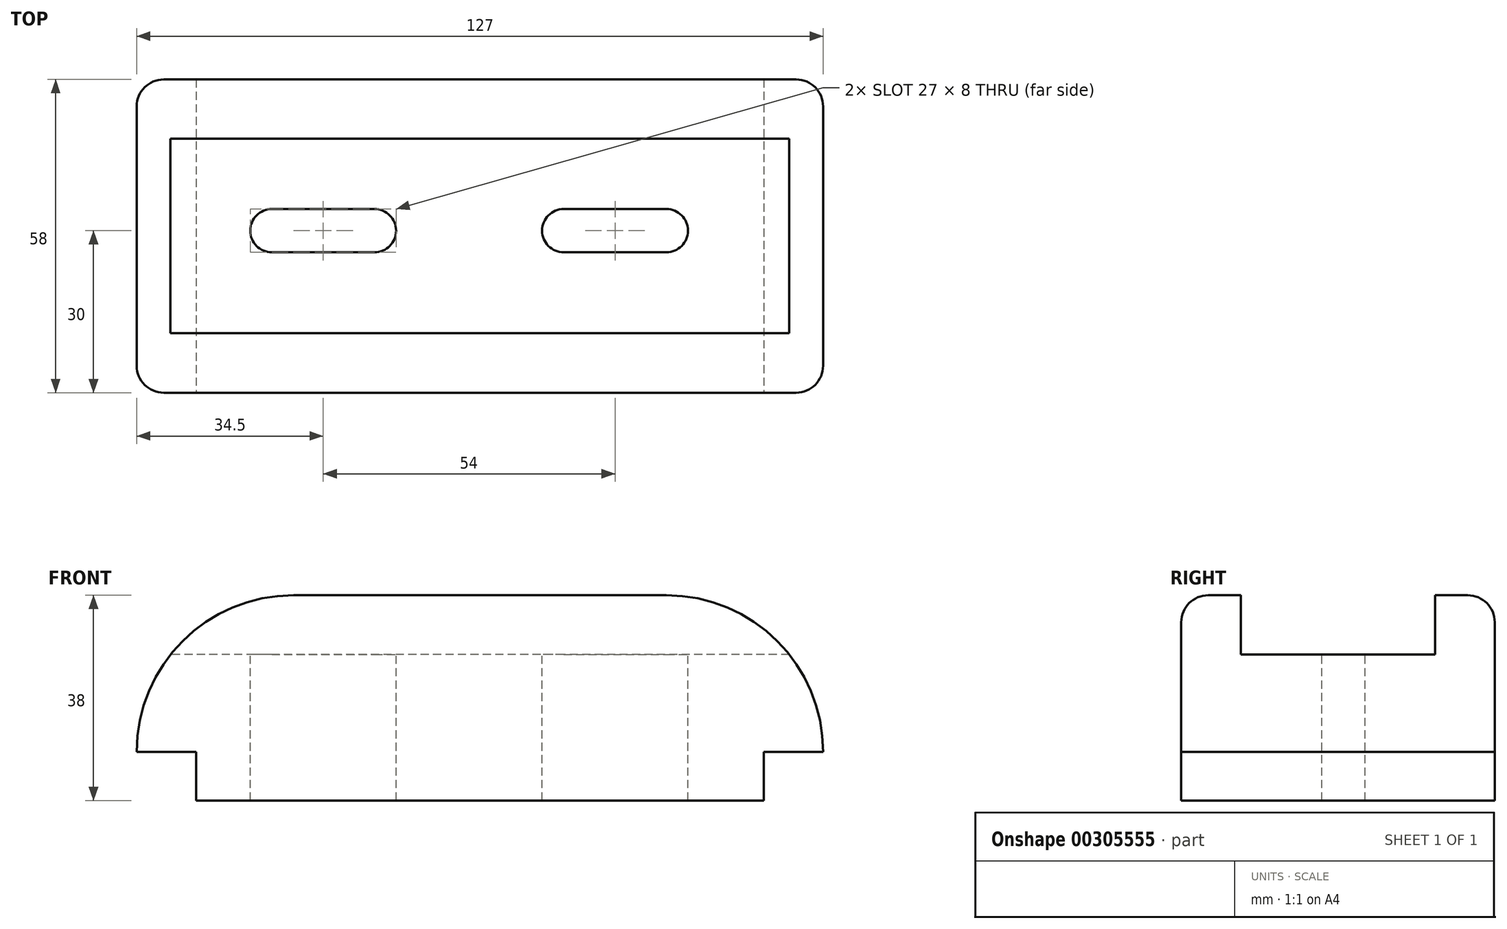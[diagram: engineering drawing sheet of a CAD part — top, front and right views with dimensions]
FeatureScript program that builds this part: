
annotation { "Feature Type Name" : "Feature", "Feature Type Description" : "" }
export const myFeature = defineFeature(function(context is Context, id is Id, definition is map)
    precondition{}
    {
        {
            var Q0;
            Q0=qCreatedBy(makeId("Front.planeOp"),FACE);
            var sketch = newSketch(context, id + "F0", { "sketchPlane" : qUnion([Q0])});
            skLineSegment(sketch, "E0.bottom", {"start": v(0, 0) * mm, "end": v(127, 0) * mm});
            skLineSegment(sketch, "E0.top", {"start": v(0, 38) * mm, "end": v(127, 38) * mm});
            skLineSegment(sketch, "E0.left", {"start": v(0, 0) * mm, "end": v(0, 38) * mm});
            skLineSegment(sketch, "E0.right", {"start": v(127, 0) * mm, "end": v(127, 38) * mm});
            skSolve(sketch);
        }
        {
            var Q0;
            Q0 = qSketchRegion(id + "F0", true);
            extrude(context, id + "F1", {"entities" : qUnion([Q0]), "depth" : 58 * mm});
        }
        {
            var Q0;
            Q0=makeQuery(id+"F1.opExtrude","SWEPT_EDGE",EDGE,{"disambiguationData":[OSD([sQuery(id+"F0.wireOp",EDGE,"E0.top"),sQuery(id+"F0.wireOp",EDGE,"E0.right")])]});
            var Q1;
            Q1=makeQuery(id+"F1.opExtrude","SWEPT_EDGE",EDGE,{"disambiguationData":[OSD([sQuery(id+"F0.wireOp",EDGE,"E0.top"),sQuery(id+"F0.wireOp",EDGE,"E0.left")])]});
            fillet(context, id + "F2", {"entities" : qUnion([Q0, Q1]), "radius" : 29 * mm, "tangentPropagation" : true, "allowEdgeOverflow" : false});
        }
        {
            var Q0;
            Q0=qCreatedBy(makeId("Right.planeOp"),FACE);
            var sketch = newSketch(context, id + "F3", { "sketchPlane" : qUnion([Q0])});
            skLineSegment(sketch, "E1.bottom", {"start": v(-47, 38) * mm, "end": v(-11, 38) * mm});
            skLineSegment(sketch, "E1.top", {"start": v(-47, 27) * mm, "end": v(-11, 27) * mm});
            skLineSegment(sketch, "E1.left", {"start": v(-47, 38) * mm, "end": v(-47, 27) * mm});
            skLineSegment(sketch, "E1.right", {"start": v(-11, 38) * mm, "end": v(-11, 27) * mm});
            skSolve(sketch);
        }
        {
            var Q0;
            Q0 = qSketchRegion(id + "F3", true);
            extrude(context, id + "F4", {"entities" : qUnion([Q0]), "operationType" : NewBodyOperationType.REMOVE, "endBound" : BoundingType.THROUGH_ALL, "depth" : 25 * mm});
        }
        {
            var Q0;
            Q0=makeQuery(id+"F1.opExtrude","CAP_FACE",FACE,{"disambiguationData":[OSD([sQuery(id+"F0.wireOp",EDGE,"E0.bottom"),sQuery(id+"F0.wireOp",EDGE,"E0.top"),sQuery(id+"F0.wireOp",EDGE,"E0.left"),sQuery(id+"F0.wireOp",EDGE,"E0.right")])],"isStart":false});
            var sketch = newSketch(context, id + "F5", { "sketchPlane" : qUnion([Q0])});
            skLineSegment(sketch, "E2.bottom", {"start": v(0, 0) * mm, "end": v(11, 0) * mm});
            skLineSegment(sketch, "E2.top", {"start": v(0, 9) * mm, "end": v(11, 9) * mm});
            skLineSegment(sketch, "E2.left", {"start": v(0, 0) * mm, "end": v(0, 9) * mm});
            skLineSegment(sketch, "E2.right", {"start": v(11, 0) * mm, "end": v(11, 9) * mm});
            skLineSegment(sketch, "E3.bottom", {"start": v(127, 0) * mm, "end": v(116, 0) * mm});
            skLineSegment(sketch, "E3.top", {"start": v(127, 9) * mm, "end": v(116, 9) * mm});
            skLineSegment(sketch, "E3.left", {"start": v(127, 0) * mm, "end": v(127, 9) * mm});
            skLineSegment(sketch, "E3.right", {"start": v(116, 0) * mm, "end": v(116, 9) * mm});
            skSolve(sketch);
        }
        {
            var Q0;
            Q0 = qSketchRegion(id + "F5", true);
            extrude(context, id + "F6", {"entities" : qUnion([Q0]), "operationType" : NewBodyOperationType.REMOVE, "endBound" : BoundingType.THROUGH_ALL, "oppositeDirection" : true, "depth" : 25 * mm});
        }
        {
            var Q0;
            Q0=makeQuery(id+"F1.opExtrude","CAP_EDGE",EDGE,{"disambiguationData":[OSD([sQuery(id+"F0.wireOp",EDGE,"E0.top")])],"isStart":false});
            var Q1;
            {var subQ0=sQuery(id+"F0.wireOp",EDGE,"E0.left");var subQ1=sQuery(id+"F0.wireOp",EDGE,"E0.top");Q1=makeQuery(id+"F2.opFillet","BLEND_EDGE",EDGE,{"blendedFrom":[makeQuery(id+"F1.opExtrude","SWEPT_EDGE",EDGE,{"disambiguationData":[OSD([subQ1,subQ0])]}),makeQuery(id+"F1.opExtrude","CAP_FACE",FACE,{"disambiguationData":[OSD([sQuery(id+"F0.wireOp",EDGE,"E0.bottom"),subQ1,subQ0,sQuery(id+"F0.wireOp",EDGE,"E0.right")])],"isStart":true})],"blendedInto":[makeQuery(id+"F1.opExtrude","CAP_FACE",FACE,{"disambiguationData":[OSD([sQuery(id+"F0.wireOp",EDGE,"E0.bottom"),subQ1,subQ0,sQuery(id+"F0.wireOp",EDGE,"E0.right")])],"isStart":true})]});}
            fillet(context, id + "F7", {"entities" : qUnion([Q0, Q1]), "radius" : 5 * mm, "tangentPropagation" : true, "allowEdgeOverflow" : false});
        }
        {
            var Q0;
            Q0=makeQuery(id+"F4.boolean.opBoolean","COPY",FACE,{"derivedFrom":makeQuery(id+"F4.opExtrude","SWEPT_FACE",FACE,{"disambiguationData":[OSD([sQuery(id+"F3.wireOp",EDGE,"E1.top")])]})});
            var sketch = newSketch(context, id + "F8", { "sketchPlane" : qUnion([Q0])});
            skArc(sketch, "E4", {"start": v(25, -24) * mm, "mid": v(21, -28) * mm, "end": v(25, -32) * mm});
            skArc(sketch, "E5", {"start": v(44, -32) * mm, "mid": v(48, -28) * mm, "end": v(44, -24) * mm});
            skLineSegment(sketch, "E6", {"start": v(25, -24) * mm, "end": v(44, -24) * mm});
            skLineSegment(sketch, "E7", {"start": v(44, -32) * mm, "end": v(25, -32) * mm});
            skArc(sketch, "E8", {"start": v(79, -24) * mm, "mid": v(75, -28) * mm, "end": v(79, -32) * mm});
            skArc(sketch, "E9", {"start": v(98, -32) * mm, "mid": v(102, -28) * mm, "end": v(98, -24) * mm});
            skLineSegment(sketch, "E10", {"start": v(79, -24) * mm, "end": v(98, -24) * mm});
            skLineSegment(sketch, "E11", {"start": v(79, -32) * mm, "end": v(98, -32) * mm});
            skSolve(sketch);
        }
        {
            var Q0;
            Q0 = qSketchRegion(id + "F8", true);
            extrude(context, id + "F9", {"entities" : qUnion([Q0]), "operationType" : NewBodyOperationType.REMOVE, "endBound" : BoundingType.THROUGH_ALL, "oppositeDirection" : true, "depth" : 25 * mm});
        }
    });
